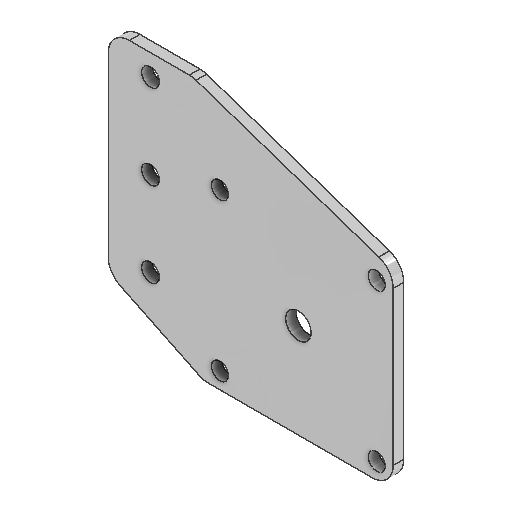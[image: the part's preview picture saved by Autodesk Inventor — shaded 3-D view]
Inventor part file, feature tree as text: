
AUTODESK INVENTOR PART (.ipt)
format: ipt  version: 2025.2 (Build 292293000, 293)  size: 153,088 bytes
history: native  units: in
note: dims shown in document units (in); Inventor stores cm internally (conversion verified against a paired STEP export)
features: extrude x1, fillet x1, sketch x1
ambient origin geometry x8: Origin, YZ Plane, XZ Plane, XY Plane, X Axis, Y Axis, Z Axis, Center Point
bodies: Solid1 (feature_tree)
feature tree (3):
  extrude  "Extrusion1"  Depth=0.25in
  fillet  "Fillet1"  Radius=0.201in
  sketch  "Sketch1"  dims[d0=2.244in d1=2.244in d3=0.201in d4=0.201in d5=0.201in d7=0.201in d15=1.122in d16=1.122in d17=2.5in d18=1.0in d19=1.0in d20=0.0in d21=0.209in d22=0.209in d23=0.209in d24=1.125in d26=0.5in d28=0.0in d29=0.0in d30=0.5in d33=3.3in d34=1.75in d35=0.125in d36=0.0in d37=0.3in d38=0.25in d39=2.6247in d40=2.6247in d41=1.3123in d42=1.3123in]
